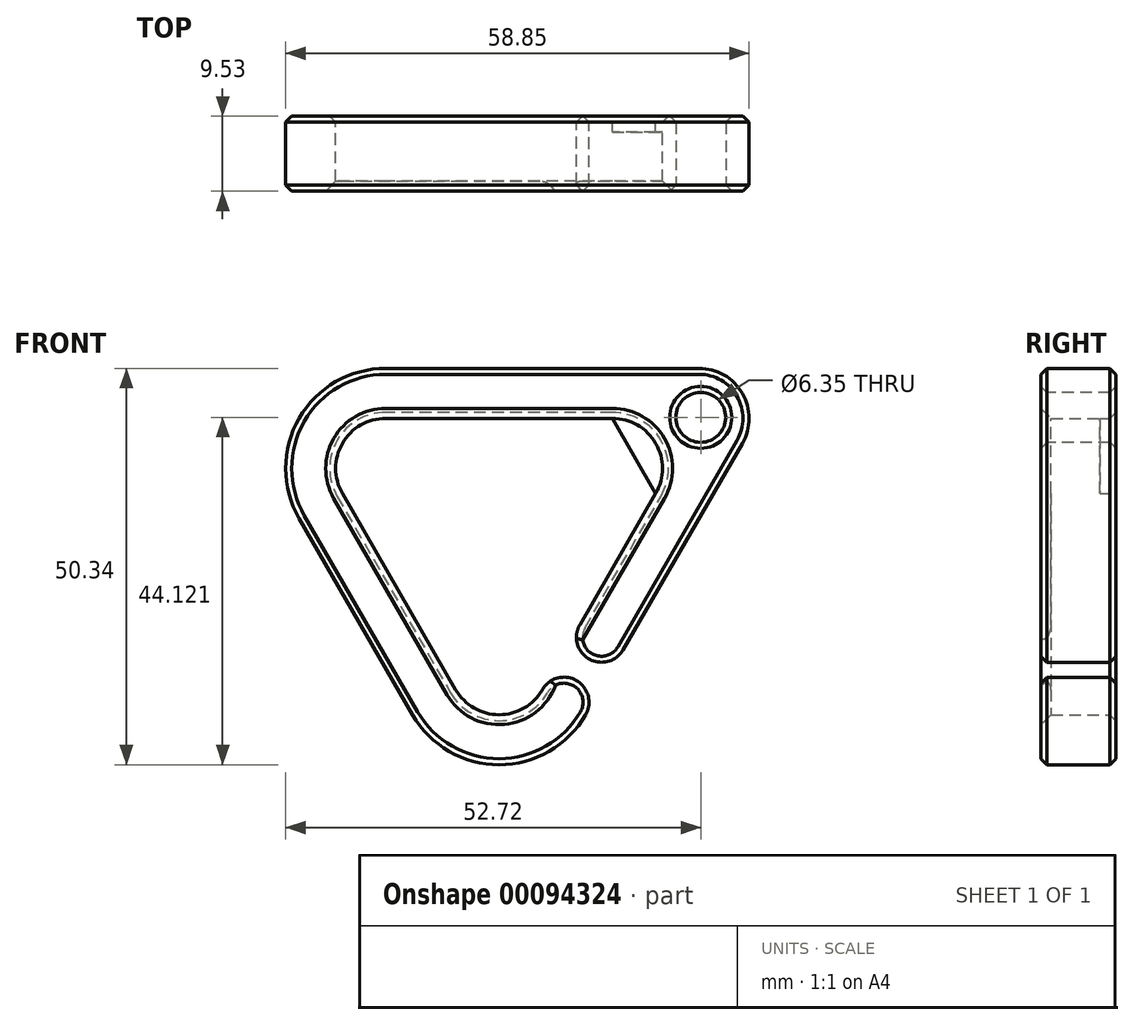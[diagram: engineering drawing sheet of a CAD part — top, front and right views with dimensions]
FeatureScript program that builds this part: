
annotation { "Feature Type Name" : "Feature", "Feature Type Description" : "" }
export const myFeature = defineFeature(function(context is Context, id is Id, definition is map)
    precondition{}
    {
        {
            var Q0;
            Q0=qCreatedBy(makeId("Front.planeOp"),FACE);
            var sketch = newSketch(context, id + "F0", { "sketchPlane" : qUnion([Q0])});
            skLineSegment(sketch, "E0", {"start": v(14.4, 44) * mm, "end": v(-14.4, 44) * mm});
            skLineSegment(sketch, "E1", {"start": v(-19.9, 34.47) * mm, "end": v(-5.5, 9.53) * mm});
            skPoint(sketch, "E2.visualSharp", {"position": v(-25.4, 44) * mm});
            skArc(sketch, "E2.filletArc", {"start": v(-14.4, 44) * mm, "mid": v(-19.9, 40.82) * mm, "end": v(-19.9, 34.47) * mm});
            skPoint(sketch, "E3.visualSharp", {"position": v(25.4, 44) * mm});
            skArc(sketch, "E3.filletArc", {"start": v(19.9, 34.47) * mm, "mid": v(19.9, 40.82) * mm, "end": v(14.4, 44) * mm});
            skPoint(sketch, "E4.visualSharp", {"position": v(0, 0) * mm});
            skArc(sketch, "E4.filletArc", {"start": v(-5.5, 9.52) * mm, "mid": v(0, 6.35) * mm, "end": v(5.5, 9.53) * mm});
            skArc(sketch, "E5.0", {"start": v(-11, 6.35) * mm, "mid": v(0, 0) * mm, "end": v(11, 6.35) * mm});
            skArc(sketch, "E5.1", {"start": v(25.4, 31.3) * mm, "mid": v(25.4, 44) * mm, "end": v(14.4, 50.34) * mm});
            skLineSegment(sketch, "E5.2", {"start": v(14.4, 50.34) * mm, "end": v(-14.4, 50.34) * mm});
            skLineSegment(sketch, "E5.3", {"start": v(15.76, 14.6) * mm, "end": v(25.4, 31.3) * mm});
            skArc(sketch, "E5.4", {"start": v(-14.4, 50.34) * mm, "mid": v(-25.4, 44) * mm, "end": v(-25.4, 31.3) * mm});
            skLineSegment(sketch, "E5.5", {"start": v(-25.4, 31.3) * mm, "end": v(-11, 6.35) * mm});
            skLineSegment(sketch, "E6", {"start": v(11, 6.35) * mm, "end": v(5.5, 9.53) * mm, "construction": true});
            skLineSegment(sketch, "E7", {"start": v(8.25, 7.94) * mm, "end": v(9.84, 10.69) * mm, "construction": true});
            skLineSegment(sketch, "E8", {"start": v(9.84, 10.69) * mm, "end": v(11.42, 13.44) * mm, "construction": true});
            skArc(sketch, "E9", {"start": v(11, 6.35) * mm, "mid": v(9.84, 10.69) * mm, "end": v(5.5, 9.53) * mm});
            skArc(sketch, "E10.MirrorCS", {"start": v(15.76, 14.6) * mm, "mid": v(11.42, 13.44) * mm, "end": v(10.26, 17.77) * mm});
            skLineSegment(sketch, "E11.trimOffspring", {"start": v(10.26, 17.77) * mm, "end": v(19.9, 34.47) * mm});
            skPoint(sketch, "E12.start.orphan", {"position": v(10.63, 12.06) * mm});
            skSolve(sketch);
        }
        {
            var Q0;
            Q0=makeQuery(id+"F0.imprint","IMPRINT",FACE,{"disambiguationData":[TD([[makeQuery(id+"F0.imprint","IMPRINT",EDGE,{"derivedFrom":sQuery(id+"F0.wireOp",EDGE,"idu5orHU-fWJF-e2BN-nVQ6-NrBh4S2ntBqF")}),-1.0]])]});
            var Q1;
            Q1=makeQuery(id+"F0.imprint","IMPRINT",FACE,{"disambiguationData":[TD([[makeQuery(id+"F0.imprint","IMPRINT",EDGE,{"derivedFrom":sQuery(id+"F0.wireOp",EDGE,"E0")}),-1.0]])]});
            extrude(context, id + "F1", {"entities" : qUnion([Q0, Q1]), "depth" : 9.52 * mm});
        }
        {
            var Q0;
            Q0=makeQuery(id+"F1.opExtrude","CAP_FACE",FACE,{"disambiguationData":[OSD([sQuery(id+"F0.wireOp",EDGE,"idu5orHU-fWJF-e2BN-nVQ6-NrBh4S2ntBqF"),sQuery(id+"F0.wireOp",EDGE,"E0"),sQuery(id+"F0.wireOp",EDGE,"E1"),sQuery(id+"F0.wireOp",EDGE,"E2.filletArc"),sQuery(id+"F0.wireOp",EDGE,"E3.filletArc"),sQuery(id+"F0.wireOp",EDGE,"E4.filletArc"),sQuery(id+"F0.wireOp",EDGE,"E5.0"),sQuery(id+"F0.wireOp",EDGE,"E5.1"),sQuery(id+"F0.wireOp",EDGE,"E5.2"),sQuery(id+"F0.wireOp",EDGE,"E5.3"),sQuery(id+"F0.wireOp",EDGE,"E5.4"),sQuery(id+"F0.wireOp",EDGE,"E5.5")])],"isStart":true});
            cPlane(context, id + "F2", {"entities" : qUnion([Q0]), "cplaneType" : CPlaneType.OFFSET, "offset" : 0.76 * mm, "oppositeDirection" : true, "width" : 152.4 * mm, "height" : 152.4 * mm});
        }
        {
            var Q0;
            Q0=makeQuery(id+"F1.opExtrude","CAP_EDGE",EDGE,{"disambiguationData":[OSD([sQuery(id+"F0.wireOp",EDGE,"E2.filletArc")])],"isStart":false});
            var Q1;
            Q1=makeQuery(id+"F1.opExtrude","CAP_EDGE",EDGE,{"disambiguationData":[OSD([sQuery(id+"F0.wireOp",EDGE,"E0")])],"isStart":false});
            var Q2;
            Q2=makeQuery(id+"F1.opExtrude","CAP_EDGE",EDGE,{"disambiguationData":[OSD([sQuery(id+"F0.wireOp",EDGE,"E3.filletArc")])],"isStart":false});
            var Q3;
            Q3=makeQuery(id+"F1.opExtrude","CAP_EDGE",EDGE,{"disambiguationData":[OSD([sQuery(id+"F0.wireOp",EDGE,"E11.trimOffspring")])],"isStart":false});
            var Q4;
            Q4=makeQuery(id+"F1.opExtrude","CAP_EDGE",EDGE,{"disambiguationData":[OSD([sQuery(id+"F0.wireOp",EDGE,"E1")])],"isStart":false});
            var Q5;
            Q5=makeQuery(id+"F1.opExtrude","CAP_EDGE",EDGE,{"disambiguationData":[OSD([sQuery(id+"F0.wireOp",EDGE,"E4.filletArc")])],"isStart":false});
            chamfer(context, id + "F3", {"entities" : qUnion([Q0, Q1, Q2, Q3, Q4, Q5]), "width" : 1.27 * mm});
        }
        {
            var Q0;
            Q0=makeQuery(id+"F1.opExtrude","CAP_FACE",FACE,{"disambiguationData":[OSD([sQuery(id+"F0.wireOp",EDGE,"E0"),sQuery(id+"F0.wireOp",EDGE,"E1"),sQuery(id+"F0.wireOp",EDGE,"E2.filletArc"),sQuery(id+"F0.wireOp",EDGE,"E3.filletArc"),sQuery(id+"F0.wireOp",EDGE,"E4.filletArc"),sQuery(id+"F0.wireOp",EDGE,"E5.0"),sQuery(id+"F0.wireOp",EDGE,"E5.1"),sQuery(id+"F0.wireOp",EDGE,"E5.2"),sQuery(id+"F0.wireOp",EDGE,"E5.3"),sQuery(id+"F0.wireOp",EDGE,"E5.4"),sQuery(id+"F0.wireOp",EDGE,"E5.5"),sQuery(id+"F0.wireOp",EDGE,"E9"),sQuery(id+"F0.wireOp",EDGE,"E10.MirrorCS"),sQuery(id+"F0.wireOp",EDGE,"E11.trimOffspring")])],"isStart":true});
            var sketch = newSketch(context, id + "F4", { "sketchPlane" : qUnion([Q0])});
            skLineSegment(sketch, "E13.0", {"start": v(-15.76, 14.6) * mm, "end": v(-25.4, 31.3) * mm});
            skPoint(sketch, "E13.1", {"position": v(-25.4, 31.3) * mm});
            skLineSegment(sketch, "E13.2", {"start": v(-14.4, 50.34) * mm, "end": v(14.4, 50.34) * mm});
            skPoint(sketch, "E13.3", {"position": v(-14.4, 50.34) * mm});
            skArc(sketch, "E13.4", {"start": v(-25.4, 31.3) * mm, "mid": v(-25.4, 44) * mm, "end": v(-14.4, 50.34) * mm});
            skLineSegment(sketch, "E14", {"start": v(-23.85, 28.6) * mm, "end": v(-30.9, 40.82) * mm});
            skLineSegment(sketch, "E15", {"start": v(-14.4, 50.34) * mm, "end": v(-25.4, 50.34) * mm});
            skPoint(sketch, "E16.visualSharp", {"position": v(-36.4, 50.34) * mm});
            skArc(sketch, "E16.filletArc", {"start": v(-25.4, 50.34) * mm, "mid": v(-30.9, 47.17) * mm, "end": v(-30.9, 40.82) * mm});
            skSolve(sketch);
        }
        {
            var Q0;
            {var subQ0=sQuery(id+"F4.wireOp",EDGE,"E13.4");Q0=makeQuery(id+"F4.imprint","IMPRINT",FACE,{"disambiguationData":[TD([[makeQuery(id+"F4.imprint","IMPRINT",EDGE,{"derivedFrom":subQ0}),1.0]])]});}
            var Q1;
            Q1=makeQuery(id+"F1.opExtrude","CAP_FACE",FACE,{"disambiguationData":[OSD([sQuery(id+"F0.wireOp",EDGE,"E0"),sQuery(id+"F0.wireOp",EDGE,"E1"),sQuery(id+"F0.wireOp",EDGE,"E2.filletArc"),sQuery(id+"F0.wireOp",EDGE,"E3.filletArc"),sQuery(id+"F0.wireOp",EDGE,"E4.filletArc"),sQuery(id+"F0.wireOp",EDGE,"E5.0"),sQuery(id+"F0.wireOp",EDGE,"E5.1"),sQuery(id+"F0.wireOp",EDGE,"E5.2"),sQuery(id+"F0.wireOp",EDGE,"E5.3"),sQuery(id+"F0.wireOp",EDGE,"E5.4"),sQuery(id+"F0.wireOp",EDGE,"E5.5"),sQuery(id+"F0.wireOp",EDGE,"E9"),sQuery(id+"F0.wireOp",EDGE,"E10.MirrorCS"),sQuery(id+"F0.wireOp",EDGE,"E11.trimOffspring")])],"isStart":false});
            extrude(context, id + "F5", {"entities" : qUnion([Q0]), "operationType" : NewBodyOperationType.ADD, "endBound" : BoundingType.UP_TO_SURFACE, "oppositeDirection" : true, "endBoundEntityFace" : qUnion([Q1]), "depth" : 25.4 * mm});
        }
        {
            var Q0;
            Q0=makeQuery(id+"F1.opExtrude","CAP_EDGE",EDGE,{"disambiguationData":[OSD([sQuery(id+"F0.wireOp",EDGE,"E10.MirrorCS")])],"isStart":false});
            var Q1;
            Q1=makeQuery(id+"F5.boolean.opBoolean","MERGE",EDGE,{"derivedFrom":[makeQuery(id+"F1.opExtrude","CAP_EDGE",EDGE,{"disambiguationData":[OSD([sQuery(id+"F0.wireOp",EDGE,"E5.3")])],"isStart":false}),makeQuery(id+"F5.opExtrude","CAP_EDGE",EDGE,{"disambiguationData":[OSD([sQuery(id+"F4.wireOp",EDGE,"E14")])],"isStart":false})]});
            var Q2;
            Q2=makeQuery(id+"F5.opExtrude","CAP_EDGE",EDGE,{"disambiguationData":[OSD([sQuery(id+"F4.wireOp",EDGE,"E16.filletArc")])],"isStart":false});
            var Q3;
            Q3=makeQuery(id+"F5.boolean.opBoolean","MERGE",EDGE,{"derivedFrom":[makeQuery(id+"F1.opExtrude","CAP_EDGE",EDGE,{"disambiguationData":[OSD([sQuery(id+"F0.wireOp",EDGE,"E5.2")])],"isStart":false}),makeQuery(id+"F5.opExtrude","CAP_EDGE",EDGE,{"disambiguationData":[OSD([sQuery(id+"F4.wireOp",EDGE,"E15")])],"isStart":false})]});
            var Q4;
            Q4=makeQuery(id+"F1.opExtrude","CAP_EDGE",EDGE,{"disambiguationData":[OSD([sQuery(id+"F0.wireOp",EDGE,"E5.4")])],"isStart":false});
            var Q5;
            Q5=makeQuery(id+"F1.opExtrude","CAP_EDGE",EDGE,{"disambiguationData":[OSD([sQuery(id+"F0.wireOp",EDGE,"E5.5")])],"isStart":false});
            var Q6;
            Q6=makeQuery(id+"F1.opExtrude","CAP_EDGE",EDGE,{"disambiguationData":[OSD([sQuery(id+"F0.wireOp",EDGE,"E5.0")])],"isStart":false});
            var Q7;
            Q7=makeQuery(id+"F1.opExtrude","CAP_EDGE",EDGE,{"disambiguationData":[OSD([sQuery(id+"F0.wireOp",EDGE,"E9")])],"isStart":false});
            var Q8;
            Q8=makeQuery(id+"F5bFKK2A3xCiJtG_1.boolean.opBoolean","COPY",EDGE,{"derivedFrom":makeQuery(id+"F5bFKK2A3xCiJtG_1.opExtrude","CAP_EDGE",EDGE,{"disambiguationData":[OSD([sQuery(id+"F6EyJjOoQRDHPNt_1.wireOp",EDGE,"doZbxLqQ-x8OJ-dWJI-eNf6-huh5UIUhoneC")])],"isStart":true})});
            chamfer(context, id + "F6", {"entities" : qUnion([Q0, Q1, Q2, Q3, Q4, Q5, Q6, Q7, Q8]), "width" : 0.76 * mm});
        }
        {
            var Q0;
            Q0=makeQuery(id+"F5.boolean.opBoolean","MERGE",FACE,{"derivedFrom":[makeQuery(id+"F1.opExtrude","CAP_FACE",FACE,{"disambiguationData":[OSD([sQuery(id+"F0.wireOp",EDGE,"E0"),sQuery(id+"F0.wireOp",EDGE,"E1"),sQuery(id+"F0.wireOp",EDGE,"E2.filletArc"),sQuery(id+"F0.wireOp",EDGE,"E3.filletArc"),sQuery(id+"F0.wireOp",EDGE,"E4.filletArc"),sQuery(id+"F0.wireOp",EDGE,"E5.0"),sQuery(id+"F0.wireOp",EDGE,"E5.1"),sQuery(id+"F0.wireOp",EDGE,"E5.2"),sQuery(id+"F0.wireOp",EDGE,"E5.3"),sQuery(id+"F0.wireOp",EDGE,"E5.4"),sQuery(id+"F0.wireOp",EDGE,"E5.5"),sQuery(id+"F0.wireOp",EDGE,"E9"),sQuery(id+"F0.wireOp",EDGE,"E10.MirrorCS"),sQuery(id+"F0.wireOp",EDGE,"E11.trimOffspring")])],"isStart":true}),makeQuery(id+"F5.opExtrude","CAP_FACE",FACE,{"disambiguationData":[OSD([sQuery(id+"F4.wireOp",EDGE,"E13.4"),sQuery(id+"F4.wireOp",EDGE,"E14"),sQuery(id+"F4.wireOp",EDGE,"E15"),sQuery(id+"F4.wireOp",EDGE,"E16.filletArc")])],"isStart":true})]});
            chamfer(context, id + "F7", {"entities" : qUnion([Q0]), "width" : 0.76 * mm, "tangentPropagation" : true});
        }
        {
            var Q0;
            Q0=makeQuery(id+"F5.boolean.opBoolean","MERGE",FACE,{"derivedFrom":[makeQuery(id+"F1.opExtrude","CAP_FACE",FACE,{"disambiguationData":[OSD([sQuery(id+"F0.wireOp",EDGE,"E0"),sQuery(id+"F0.wireOp",EDGE,"E1"),sQuery(id+"F0.wireOp",EDGE,"E2.filletArc"),sQuery(id+"F0.wireOp",EDGE,"E3.filletArc"),sQuery(id+"F0.wireOp",EDGE,"E4.filletArc"),sQuery(id+"F0.wireOp",EDGE,"E5.0"),sQuery(id+"F0.wireOp",EDGE,"E5.1"),sQuery(id+"F0.wireOp",EDGE,"E5.2"),sQuery(id+"F0.wireOp",EDGE,"E5.3"),sQuery(id+"F0.wireOp",EDGE,"E5.4"),sQuery(id+"F0.wireOp",EDGE,"E5.5"),sQuery(id+"F0.wireOp",EDGE,"E9"),sQuery(id+"F0.wireOp",EDGE,"E10.MirrorCS"),sQuery(id+"F0.wireOp",EDGE,"E11.trimOffspring")])],"isStart":false}),makeQuery(id+"F5.opExtrude","CAP_FACE",FACE,{"disambiguationData":[OSD([sQuery(id+"F4.wireOp",EDGE,"E13.4"),sQuery(id+"F4.wireOp",EDGE,"E14"),sQuery(id+"F4.wireOp",EDGE,"E15"),sQuery(id+"F4.wireOp",EDGE,"E16.filletArc")])],"isStart":false})]});
            var sketch = newSketch(context, id + "F8", { "sketchPlane" : qUnion([Q0])});
            skLineSegment(sketch, "E17", {"start": v(21, 41.45) * mm, "end": v(30.24, 46.79) * mm, "construction": true});
            skCircle(sketch, "E18", {"center": v(25.62, 44.12) * mm, "radius": 3.18 * mm});
            skSolve(sketch);
        }
        {
            var Q0;
            Q0=makeQuery(id+"F8.imprint","IMPRINT",FACE,{"disambiguationData":[TD([[makeQuery(id+"F8.imprint","IMPRINT",EDGE,{"derivedFrom":sQuery(id+"F8.wireOp",EDGE,"E18")}),1.0]])]});
            extrude(context, id + "F9", {"entities" : qUnion([Q0]), "operationType" : NewBodyOperationType.REMOVE, "endBound" : BoundingType.THROUGH_ALL, "oppositeDirection" : true, "depth" : 25.4 * mm});
        }
        {
            var Q0;
            Q0=makeQuery(id+"F9.boolean.opBoolean","COPY",FACE,{"derivedFrom":makeQuery(id+"F9.opExtrude","SWEPT_FACE",FACE,{"disambiguationData":[OSD([sQuery(id+"F8.wireOp",EDGE,"E18")])]})});
            chamfer(context, id + "F10", {"entities" : qUnion([Q0]), "width" : 0.76 * mm, "tangentPropagation" : true});
        }
        {
            var Q0;
            Q0=qCreatedBy(id+"F2.planeOp",FACE);
            var sketch = newSketch(context, id + "F11", { "sketchPlane" : qUnion([Q0])});
            skPoint(sketch, "E19.0", {"position": v(-19.9, 34.47) * mm});
            skPoint(sketch, "E19.1", {"position": v(-14.4, 44) * mm});
            skArc(sketch, "E19.2", {"start": v(-14.4, 44) * mm, "mid": v(-19.9, 40.82) * mm, "end": v(-19.9, 34.47) * mm});
            skLineSegment(sketch, "E20", {"start": v(-19.9, 34.47) * mm, "end": v(-14.4, 44) * mm});
            skSolve(sketch);
        }
        {
            var Q0;
            Q0 = qSketchRegion(id + "F11", true);
            extrude(context, id + "F12", {"entities" : qUnion([Q0]), "operationType" : NewBodyOperationType.ADD, "oppositeDirection" : true, "depth" : 1.27 * mm});
        }
    });
